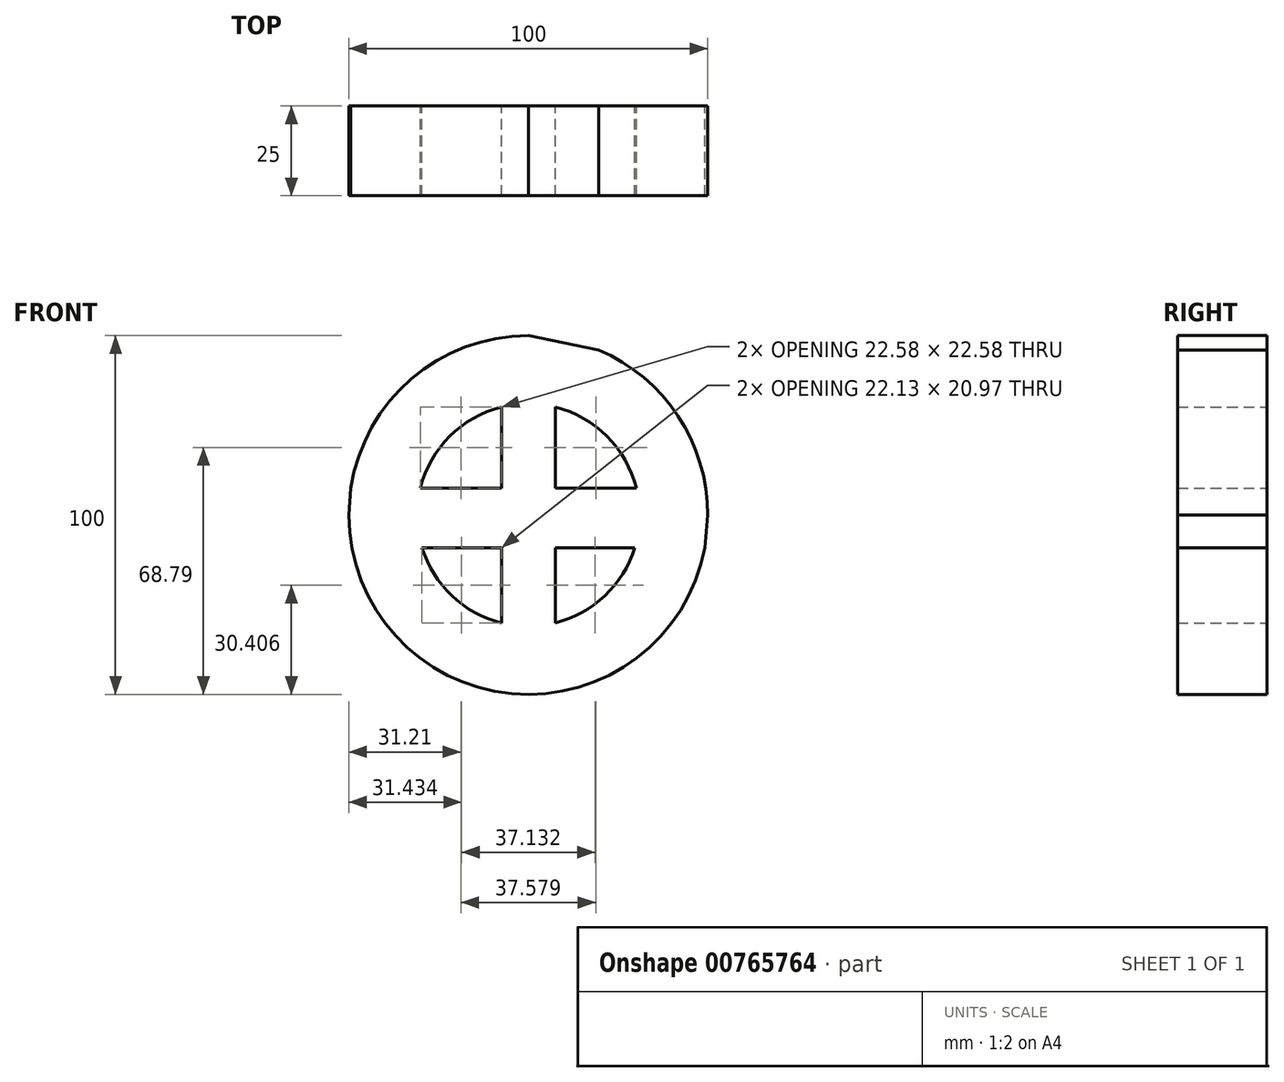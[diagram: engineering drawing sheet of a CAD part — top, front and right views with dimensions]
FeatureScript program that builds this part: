
annotation { "Feature Type Name" : "Feature", "Feature Type Description" : "" }
export const myFeature = defineFeature(function(context is Context, id is Id, definition is map)
    precondition{}
    {
        {
            var Q0;
            Q0=qCreatedBy(makeId("Front.planeOp"),FACE);
            var sketch = newSketch(context, id + "F0", { "sketchPlane" : qUnion([Q0])});
            skCircle(sketch, "E0", {"center": v(0, 0) * mm, "radius": 50 * mm});
            skLineSegment(sketch, "E1.bottom", {"start": v(-110, 110) * mm, "end": v(110, 110) * mm});
            skLineSegment(sketch, "E1.top", {"start": v(-110, -110) * mm, "end": v(110, -110) * mm});
            skLineSegment(sketch, "E1.left", {"start": v(-110, 110) * mm, "end": v(-110, -110) * mm});
            skLineSegment(sketch, "E1.right", {"start": v(110, 110) * mm, "end": v(110, -110) * mm});
            skCircle(sketch, "E2", {"center": v(0, 0) * mm, "radius": 31 * mm});
            skCircle(sketch, "E3", {"center": v(0, 0) * mm, "radius": 7.5 * mm});
            skCircle(sketch, "E4", {"center": v(0, 0) * mm, "radius": 2.5 * mm});
            skLineSegment(sketch, "E5", {"start": v(0, 50) * mm, "end": v(62.18, 37.3) * mm});
            skLineSegment(sketch, "E6", {"start": v(0, 0) * mm, "end": v(-50, 0) * mm});
            skLineSegment(sketch, "E7", {"start": v(-50, 0) * mm, "end": v(50, 0) * mm});
            skLineSegment(sketch, "E8", {"start": v(50, 0) * mm, "end": v(0, 0) * mm});
            skLineSegment(sketch, "E9", {"start": v(0, -50) * mm, "end": v(0, 0) * mm});
            skLineSegment(sketch, "E10", {"start": v(0, 50) * mm, "end": v(0, 0) * mm});
            skLineSegment(sketch, "E11", {"start": v(7.5, 0) * mm, "end": v(7.5, 49.43) * mm});
            skLineSegment(sketch, "E12", {"start": v(7.5, 0) * mm, "end": v(-7.5, 0) * mm});
            skLineSegment(sketch, "E13", {"start": v(-7.5, 0) * mm, "end": v(-7.5, 49.43) * mm});
            skLineSegment(sketch, "E14", {"start": v(-7.5, 49.43) * mm, "end": v(-7.5, 0) * mm});
            skLineSegment(sketch, "E15", {"start": v(0, 0) * mm, "end": v(0, 7.5) * mm});
            skLineSegment(sketch, "E16", {"start": v(0, 7.5) * mm, "end": v(-49.43, 7.5) * mm});
            skLineSegment(sketch, "E17", {"start": v(-49.43, 7.5) * mm, "end": v(-50, 0) * mm});
            skLineSegment(sketch, "E18", {"start": v(-49.16, -9.1) * mm, "end": v(0, -9.1) * mm});
            skLineSegment(sketch, "E19", {"start": v(0, -9.1) * mm, "end": v(49.16, -9.1) * mm});
            skLineSegment(sketch, "E20", {"start": v(49.16, -9.1) * mm, "end": v(50, 0) * mm});
            skLineSegment(sketch, "E21", {"start": v(0, 7.5) * mm, "end": v(50, 7.5) * mm});
            skLineSegment(sketch, "E22", {"start": v(-7.5, 0) * mm, "end": v(-7.5, -49.43) * mm});
            skLineSegment(sketch, "E23", {"start": v(-7.5, -49.43) * mm, "end": v(-7.5, 0) * mm});
            skLineSegment(sketch, "E24", {"start": v(7.5, 0) * mm, "end": v(7.5, -49.43) * mm});
            skSolve(sketch);
        }
        {
            var Q0;
            {var subQ3=sQuery(id+"F0.wireOp",EDGE,"E13");var subQ5=sQuery(id+"F0.wireOp",EDGE,"E2");var subQ6=makeQuery(id+"F0.imprint","INTERSECT",VERTEX,{"derivedFrom":[subQ5,subQ3]});Q0=makeQuery(id+"F0.imprint","IMPRINT",FACE,{"disambiguationData":[TD([[makeQuery(id+"F0.imprint","IMPRINT",EDGE,{"disambiguationData":[TD([[subQ6,-1.0]])],"derivedFrom":subQ5}),-1.0]])]});}
            var Q1;
            {var subQ1=sQuery(id+"F0.wireOp",EDGE,"E5");var subQ5=sQuery(id+"F0.wireOp",EDGE,"E0");var subQ6=makeQuery(id+"F0.imprint","INTERSECT",VERTEX,{"derivedFrom":[subQ5,subQ1]});Q1=makeQuery(id+"F0.imprint","IMPRINT",FACE,{"disambiguationData":[TD([[makeQuery(id+"F0.imprint","IMPRINT",EDGE,{"disambiguationData":[TD([[subQ6,1.0]])],"derivedFrom":subQ5}),1.0]])]});}
            var Q2;
            {var subQ3=sQuery(id+"F0.wireOp",EDGE,"E24");var subQ5=sQuery(id+"F0.wireOp",EDGE,"E2");var subQ7=makeQuery(id+"F0.imprint","INTERSECT",VERTEX,{"derivedFrom":[subQ5,subQ3]});Q2=makeQuery(id+"F0.imprint","IMPRINT",FACE,{"disambiguationData":[TD([[makeQuery(id+"F0.imprint","IMPRINT",EDGE,{"disambiguationData":[TD([[subQ7,-1.0]])],"derivedFrom":subQ5}),-1.0]])]});}
            var Q3;
            {var subQ5=sQuery(id+"F0.wireOp",EDGE,"E20");Q3=makeQuery(id+"F0.imprint","IMPRINT",FACE,{"disambiguationData":[TD([[makeQuery(id+"F0.imprint","IMPRINT",EDGE,{"derivedFrom":subQ5}),1.0]])]});}
            var Q4;
            {var subQ0=sQuery(id+"F0.wireOp",EDGE,"E7");var subQ5=sQuery(id+"F0.wireOp",EDGE,"E2");var subQ6=makeQuery(id+"F0.imprint","INTERSECT",VERTEX,{"derivedFrom":[subQ5,subQ0]});Q4=makeQuery(id+"F0.imprint","IMPRINT",FACE,{"disambiguationData":[TD([[makeQuery(id+"F0.imprint","IMPRINT",EDGE,{"disambiguationData":[TD([[subQ6,-1.0]])],"derivedFrom":subQ5}),-1.0]])]});}
            var Q5;
            {var subQ0=sQuery(id+"F0.wireOp",EDGE,"E10");var subQ1=sQuery(id+"F0.wireOp",EDGE,"E2");var subQ2=makeQuery(id+"F0.imprint","INTERSECT",VERTEX,{"derivedFrom":[subQ1,subQ0]});Q5=makeQuery(id+"F0.imprint","IMPRINT",FACE,{"disambiguationData":[TD([[makeQuery(id+"F0.imprint","IMPRINT",EDGE,{"disambiguationData":[TD([[subQ2,1.0]])],"derivedFrom":subQ1}),-1.0]])]});}
            var Q6;
            {var subQ5=sQuery(id+"F0.wireOp",EDGE,"E17");Q6=makeQuery(id+"F0.imprint","IMPRINT",FACE,{"disambiguationData":[TD([[makeQuery(id+"F0.imprint","IMPRINT",EDGE,{"derivedFrom":subQ5}),1.0]])]});}
            var Q7;
            {var subQ3=sQuery(id+"F0.wireOp",EDGE,"E18");var subQ5=sQuery(id+"F0.wireOp",EDGE,"E2");var subQ7=makeQuery(id+"F0.imprint","INTERSECT",VERTEX,{"derivedFrom":[subQ5,subQ3]});Q7=makeQuery(id+"F0.imprint","IMPRINT",FACE,{"disambiguationData":[TD([[makeQuery(id+"F0.imprint","IMPRINT",EDGE,{"disambiguationData":[TD([[subQ7,1.0]])],"derivedFrom":subQ5}),-1.0]])]});}
            var Q8;
            {var subQ0=sQuery(id+"F0.wireOp",EDGE,"E18");var subQ1=sQuery(id+"F0.wireOp",EDGE,"E0");var subQ2=makeQuery(id+"F0.imprint","INTERSECT",VERTEX,{"derivedFrom":[subQ1,subQ0]});Q8=makeQuery(id+"F0.imprint","IMPRINT",FACE,{"disambiguationData":[TD([[makeQuery(id+"F0.imprint","IMPRINT",EDGE,{"disambiguationData":[TD([[subQ2,-1.0]])],"derivedFrom":subQ1}),1.0]])]});}
            var Q9;
            {var subQ0=sQuery(id+"F0.wireOp",EDGE,"E9");var subQ1=sQuery(id+"F0.wireOp",EDGE,"E0");var subQ2=makeQuery(id+"F0.imprint","INTERSECT",VERTEX,{"derivedFrom":[subQ1,subQ0]});Q9=makeQuery(id+"F0.imprint","IMPRINT",FACE,{"disambiguationData":[TD([[makeQuery(id+"F0.imprint","IMPRINT",EDGE,{"disambiguationData":[TD([[subQ2,1.0]])],"derivedFrom":subQ1}),1.0]])]});}
            var Q10;
            {var subQ0=sQuery(id+"F0.wireOp",EDGE,"E24");var subQ1=sQuery(id+"F0.wireOp",EDGE,"E0");var subQ2=makeQuery(id+"F0.imprint","INTERSECT",VERTEX,{"derivedFrom":[subQ1,subQ0]});Q10=makeQuery(id+"F0.imprint","IMPRINT",FACE,{"disambiguationData":[TD([[makeQuery(id+"F0.imprint","IMPRINT",EDGE,{"disambiguationData":[TD([[subQ2,1.0]])],"derivedFrom":subQ1}),1.0]])]});}
            var Q11;
            {var subQ3=sQuery(id+"F0.wireOp",EDGE,"E10");var subQ5=sQuery(id+"F0.wireOp",EDGE,"E2");var subQ6=makeQuery(id+"F0.imprint","INTERSECT",VERTEX,{"derivedFrom":[subQ5,subQ3]});Q11=makeQuery(id+"F0.imprint","IMPRINT",FACE,{"disambiguationData":[TD([[makeQuery(id+"F0.imprint","IMPRINT",EDGE,{"disambiguationData":[TD([[subQ6,-1.0]])],"derivedFrom":subQ5}),-1.0]])]});}
            var Q12;
            {var subQ0=sQuery(id+"F0.wireOp",EDGE,"E16");var subQ1=sQuery(id+"F0.wireOp",EDGE,"E2");var subQ2=makeQuery(id+"F0.imprint","INTERSECT",VERTEX,{"derivedFrom":[subQ1,subQ0]});Q12=makeQuery(id+"F0.imprint","IMPRINT",FACE,{"disambiguationData":[TD([[makeQuery(id+"F0.imprint","IMPRINT",EDGE,{"disambiguationData":[TD([[subQ2,-1.0]])],"derivedFrom":subQ1}),1.0]])]});}
            var Q13;
            {var subQ0=sQuery(id+"F0.wireOp",EDGE,"E18");var subQ1=sQuery(id+"F0.wireOp",EDGE,"E2");var subQ2=makeQuery(id+"F0.imprint","INTERSECT",VERTEX,{"derivedFrom":[subQ1,subQ0]});Q13=makeQuery(id+"F0.imprint","IMPRINT",FACE,{"disambiguationData":[TD([[makeQuery(id+"F0.imprint","IMPRINT",EDGE,{"disambiguationData":[TD([[subQ2,1.0]])],"derivedFrom":subQ1}),1.0]])]});}
            var Q14;
            {var subQ0=sQuery(id+"F0.wireOp",EDGE,"E7");var subQ1=sQuery(id+"F0.wireOp",EDGE,"E2");var subQ2=makeQuery(id+"F0.imprint","INTERSECT",VERTEX,{"derivedFrom":[subQ1,subQ0]});Q14=makeQuery(id+"F0.imprint","IMPRINT",FACE,{"disambiguationData":[TD([[makeQuery(id+"F0.imprint","IMPRINT",EDGE,{"disambiguationData":[TD([[subQ2,-1.0]])],"derivedFrom":subQ1}),1.0]])]});}
            var Q15;
            {var subQ0=sQuery(id+"F0.wireOp",EDGE,"E19");var subQ1=sQuery(id+"F0.wireOp",EDGE,"E2");var subQ2=makeQuery(id+"F0.imprint","INTERSECT",VERTEX,{"derivedFrom":[subQ1,subQ0]});Q15=makeQuery(id+"F0.imprint","IMPRINT",FACE,{"disambiguationData":[TD([[makeQuery(id+"F0.imprint","IMPRINT",EDGE,{"disambiguationData":[TD([[subQ2,-1.0]])],"derivedFrom":subQ1}),1.0]])]});}
            var Q16;
            {var subQ0=sQuery(id+"F0.wireOp",EDGE,"E7");var subQ5=sQuery(id+"F0.wireOp",EDGE,"E4");var subQ6=makeQuery(id+"F0.imprint","INTERSECT",VERTEX,{"derivedFrom":[subQ5,subQ0]});Q16=makeQuery(id+"F0.imprint","IMPRINT",FACE,{"disambiguationData":[TD([[makeQuery(id+"F0.imprint","IMPRINT",EDGE,{"disambiguationData":[TD([[subQ6,-1.0]])],"derivedFrom":subQ5}),-1.0]])]});}
            var Q17;
            {var subQ0=sQuery(id+"F0.wireOp",EDGE,"E6");var subQ5=sQuery(id+"F0.wireOp",EDGE,"E4");var subQ6=makeQuery(id+"F0.imprint","INTERSECT",VERTEX,{"derivedFrom":[subQ5,subQ0]});Q17=makeQuery(id+"F0.imprint","IMPRINT",FACE,{"disambiguationData":[TD([[makeQuery(id+"F0.imprint","IMPRINT",EDGE,{"disambiguationData":[TD([[subQ6,1.0]])],"derivedFrom":subQ5}),-1.0]])]});}
            var Q18;
            {var subQ0=sQuery(id+"F0.wireOp",EDGE,"E7");var subQ5=sQuery(id+"F0.wireOp",EDGE,"E4");var subQ7=makeQuery(id+"F0.imprint","INTERSECT",VERTEX,{"derivedFrom":[subQ5,subQ0]});Q18=makeQuery(id+"F0.imprint","IMPRINT",FACE,{"disambiguationData":[TD([[makeQuery(id+"F0.imprint","IMPRINT",EDGE,{"disambiguationData":[TD([[subQ7,1.0]])],"derivedFrom":subQ5}),-1.0]])]});}
            var Q19;
            {var subQ0=sQuery(id+"F0.wireOp",EDGE,"E6");var subQ5=sQuery(id+"F0.wireOp",EDGE,"E4");var subQ6=makeQuery(id+"F0.imprint","INTERSECT",VERTEX,{"derivedFrom":[subQ5,subQ0]});Q19=makeQuery(id+"F0.imprint","IMPRINT",FACE,{"disambiguationData":[TD([[makeQuery(id+"F0.imprint","IMPRINT",EDGE,{"disambiguationData":[TD([[subQ6,-1.0]])],"derivedFrom":subQ5}),-1.0]])]});}
            var Q20;
            {var subQ0=sQuery(id+"F0.wireOp",EDGE,"E6");var subQ1=sQuery(id+"F0.wireOp",EDGE,"E4");var subQ2=makeQuery(id+"F0.imprint","INTERSECT",VERTEX,{"derivedFrom":[subQ1,subQ0]});Q20=makeQuery(id+"F0.imprint","IMPRINT",FACE,{"disambiguationData":[TD([[makeQuery(id+"F0.imprint","IMPRINT",EDGE,{"disambiguationData":[TD([[subQ2,-1.0]])],"derivedFrom":subQ1}),1.0]])]});}
            var Q21;
            {var subQ0=sQuery(id+"F0.wireOp",EDGE,"E7");var subQ1=sQuery(id+"F0.wireOp",EDGE,"E4");var subQ2=makeQuery(id+"F0.imprint","INTERSECT",VERTEX,{"derivedFrom":[subQ1,subQ0]});Q21=makeQuery(id+"F0.imprint","IMPRINT",FACE,{"disambiguationData":[TD([[makeQuery(id+"F0.imprint","IMPRINT",EDGE,{"disambiguationData":[TD([[subQ2,1.0]])],"derivedFrom":subQ1}),1.0]])]});}
            var Q22;
            {var subQ0=sQuery(id+"F0.wireOp",EDGE,"E7");var subQ1=sQuery(id+"F0.wireOp",EDGE,"E4");var subQ2=makeQuery(id+"F0.imprint","INTERSECT",VERTEX,{"derivedFrom":[subQ1,subQ0]});Q22=makeQuery(id+"F0.imprint","IMPRINT",FACE,{"disambiguationData":[TD([[makeQuery(id+"F0.imprint","IMPRINT",EDGE,{"disambiguationData":[TD([[subQ2,-1.0]])],"derivedFrom":subQ1}),1.0]])]});}
            var Q23;
            {var subQ0=sQuery(id+"F0.wireOp",EDGE,"E6");var subQ1=sQuery(id+"F0.wireOp",EDGE,"E4");var subQ2=makeQuery(id+"F0.imprint","INTERSECT",VERTEX,{"derivedFrom":[subQ1,subQ0]});Q23=makeQuery(id+"F0.imprint","IMPRINT",FACE,{"disambiguationData":[TD([[makeQuery(id+"F0.imprint","IMPRINT",EDGE,{"disambiguationData":[TD([[subQ2,1.0]])],"derivedFrom":subQ1}),1.0]])]});}
            var Q24;
            {var subQ0=sQuery(id+"F0.wireOp",EDGE,"E11");var subQ3=sQuery(id+"F0.wireOp",EDGE,"E21");var subQ5=makeQuery(id+"F0.imprint","INTERSECT",VERTEX,{"derivedFrom":[subQ0,subQ3]});Q24=makeQuery(id+"F0.imprint","IMPRINT",FACE,{"disambiguationData":[TD([[makeQuery(id+"F0.imprint","IMPRINT",EDGE,{"disambiguationData":[TD([[subQ5,1.0]])],"derivedFrom":subQ0}),1.0]])]});}
            var Q25;
            {var subQ0=sQuery(id+"F0.wireOp",EDGE,"E13");var subQ3=sQuery(id+"F0.wireOp",EDGE,"E16");var subQ5=makeQuery(id+"F0.imprint","INTERSECT",VERTEX,{"derivedFrom":[subQ0,subQ3]});Q25=makeQuery(id+"F0.imprint","IMPRINT",FACE,{"disambiguationData":[TD([[makeQuery(id+"F0.imprint","IMPRINT",EDGE,{"disambiguationData":[TD([[subQ5,1.0]])],"derivedFrom":subQ0}),-1.0]])]});}
            var Q26;
            {var subQ1=sQuery(id+"F0.wireOp",EDGE,"E3");var subQ3=sQuery(id+"F0.wireOp",EDGE,"E9");var subQ4=makeQuery(id+"F0.imprint","INTERSECT",VERTEX,{"derivedFrom":[subQ1,subQ3]});Q26=makeQuery(id+"F0.imprint","IMPRINT",FACE,{"disambiguationData":[TD([[makeQuery(id+"F0.imprint","IMPRINT",EDGE,{"disambiguationData":[TD([[subQ4,1.0]])],"derivedFrom":subQ3}),1.0]])]});}
            var Q27;
            {var subQ1=sQuery(id+"F0.wireOp",EDGE,"E3");var subQ3=sQuery(id+"F0.wireOp",EDGE,"E9");var subQ4=makeQuery(id+"F0.imprint","INTERSECT",VERTEX,{"derivedFrom":[subQ1,subQ3]});Q27=makeQuery(id+"F0.imprint","IMPRINT",FACE,{"disambiguationData":[TD([[makeQuery(id+"F0.imprint","IMPRINT",EDGE,{"disambiguationData":[TD([[subQ4,1.0]])],"derivedFrom":subQ3}),-1.0]])]});}
            var Q28;
            {var subQ0=sQuery(id+"F0.wireOp",EDGE,"E10");var subQ1=sQuery(id+"F0.wireOp",EDGE,"E2");var subQ2=makeQuery(id+"F0.imprint","INTERSECT",VERTEX,{"derivedFrom":[subQ1,subQ0]});Q28=makeQuery(id+"F0.imprint","IMPRINT",FACE,{"disambiguationData":[TD([[makeQuery(id+"F0.imprint","IMPRINT",EDGE,{"disambiguationData":[TD([[subQ2,-1.0]])],"derivedFrom":subQ1}),1.0]])]});}
            var Q29;
            {var subQ0=sQuery(id+"F0.wireOp",EDGE,"E10");var subQ1=sQuery(id+"F0.wireOp",EDGE,"E2");var subQ2=makeQuery(id+"F0.imprint","INTERSECT",VERTEX,{"derivedFrom":[subQ1,subQ0]});Q29=makeQuery(id+"F0.imprint","IMPRINT",FACE,{"disambiguationData":[TD([[makeQuery(id+"F0.imprint","IMPRINT",EDGE,{"disambiguationData":[TD([[subQ2,1.0]])],"derivedFrom":subQ1}),1.0]])]});}
            var Q30;
            {var subQ0=sQuery(id+"F0.wireOp",EDGE,"E9");var subQ1=sQuery(id+"F0.wireOp",EDGE,"E2");var subQ2=makeQuery(id+"F0.imprint","INTERSECT",VERTEX,{"derivedFrom":[subQ1,subQ0]});Q30=makeQuery(id+"F0.imprint","IMPRINT",FACE,{"disambiguationData":[TD([[makeQuery(id+"F0.imprint","IMPRINT",EDGE,{"disambiguationData":[TD([[subQ2,1.0]])],"derivedFrom":subQ1}),1.0]])]});}
            var Q31;
            {var subQ0=sQuery(id+"F0.wireOp",EDGE,"E9");var subQ1=sQuery(id+"F0.wireOp",EDGE,"E2");var subQ2=makeQuery(id+"F0.imprint","INTERSECT",VERTEX,{"derivedFrom":[subQ1,subQ0]});Q31=makeQuery(id+"F0.imprint","IMPRINT",FACE,{"disambiguationData":[TD([[makeQuery(id+"F0.imprint","IMPRINT",EDGE,{"disambiguationData":[TD([[subQ2,-1.0]])],"derivedFrom":subQ1}),1.0]])]});}
            extrude(context, id + "F1", {"entities" : qUnion([Q0, Q1, Q2, Q3, Q4, Q5, Q6, Q7, Q8, Q9, Q10, Q11, Q12, Q13, Q14, Q15, Q16, Q17, Q18, Q19, Q20, Q21, Q22, Q23, Q24, Q25, Q26, Q27, Q28, Q29, Q30, Q31]), "depth" : 25 * mm, "offsetDistance" : 25 * mm});
        }
    });
